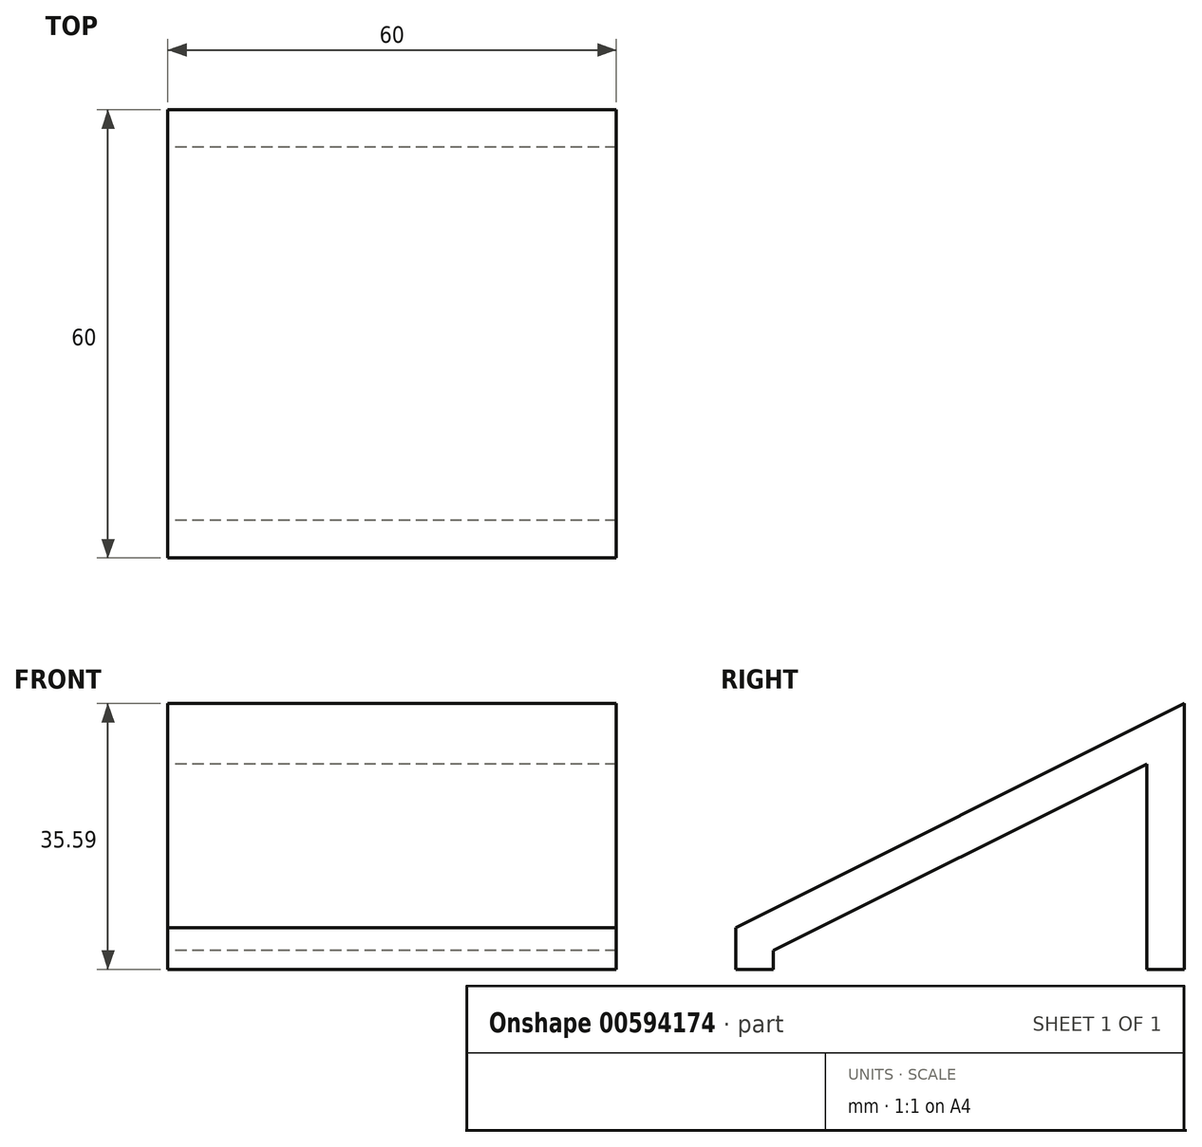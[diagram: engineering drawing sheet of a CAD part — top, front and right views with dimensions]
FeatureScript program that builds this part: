
annotation { "Feature Type Name" : "Feature", "Feature Type Description" : "" }
export const myFeature = defineFeature(function(context is Context, id is Id, definition is map)
    precondition{}
    {
        {
            var Q0;
            Q0=qCreatedBy(makeId("Right.planeOp"),FACE);
            var sketch = newSketch(context, id + "F0", { "sketchPlane" : qUnion([Q0])});
            skLineSegment(sketch, "E0", {"start": v(0, 0) * mm, "end": v(0, 30) * mm});
            skLineSegment(sketch, "E1", {"start": v(0, 30) * mm, "end": v(-60, 0) * mm});
            skLineSegment(sketch, "E2", {"start": v(0, 0) * mm, "end": v(-5, 0) * mm});
            skLineSegment(sketch, "E3", {"start": v(-5, 0) * mm, "end": v(-5, 27.5) * mm});
            skLineSegment(sketch, "E4", {"start": v(-60, 0) * mm, "end": v(-55, 0) * mm});
            skLineSegment(sketch, "E5", {"start": v(-55, 0) * mm, "end": v(-55, 2.5) * mm});
            skLineSegment(sketch, "E6", {"start": v(-60, 0) * mm, "end": v(-60, 5.6) * mm});
            skLineSegment(sketch, "E7", {"start": v(-60, 5.6) * mm, "end": v(0, 35.6) * mm});
            skLineSegment(sketch, "E8", {"start": v(0, 35.6) * mm, "end": v(0, 30) * mm});
            skSolve(sketch);
        }
        {
            var Q0;
            Q0 = qSketchRegion(id + "F0", true);
            extrude(context, id + "F1", {"entities" : qUnion([Q0]), "depth" : 60 * mm, "offsetDistance" : 25 * mm});
        }
    });
